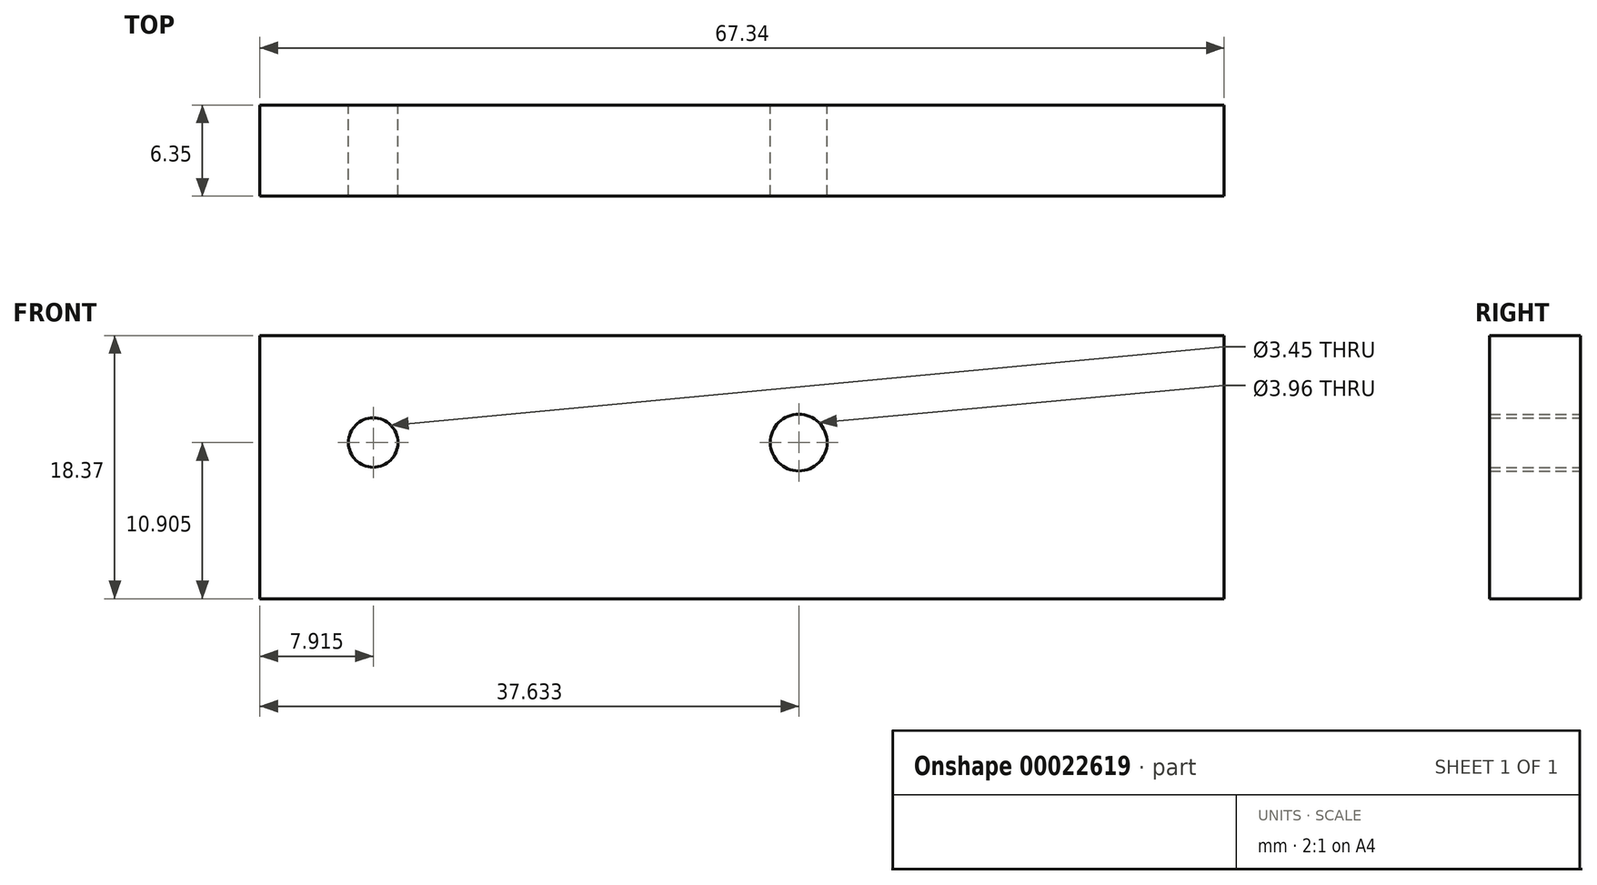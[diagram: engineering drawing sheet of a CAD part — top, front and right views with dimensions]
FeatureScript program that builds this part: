
annotation { "Feature Type Name" : "Feature", "Feature Type Description" : "" }
export const myFeature = defineFeature(function(context is Context, id is Id, definition is map)
    precondition{}
    {
        {
            var Q0;
            Q0=qCreatedBy(makeId("Front.planeOp"),FACE);
            var sketch = newSketch(context, id + "F0", { "sketchPlane" : qUnion([Q0])});
            skCircle(sketch, "E0", {"center": v(-31.44, 26.57) * mm, "radius": 1.73 * mm});
            skCircle(sketch, "E1", {"center": v(-1.72, 26.57) * mm, "radius": 1.98 * mm});
            skLineSegment(sketch, "E2.rect.bottom", {"start": v(-39.35, 34.03) * mm, "end": v(27.99, 34.03) * mm});
            skLineSegment(sketch, "E2.rect.top", {"start": v(-39.35, 15.66) * mm, "end": v(27.99, 15.66) * mm});
            skLineSegment(sketch, "E2.rect.left", {"start": v(-39.35, 34.03) * mm, "end": v(-39.35, 15.66) * mm});
            skLineSegment(sketch, "E2.rect.right", {"start": v(27.99, 34.03) * mm, "end": v(27.99, 15.66) * mm});
            skPoint(sketch, "E2.rect.middle", {"position": v(-5.68, 24.84) * mm});
            skSolve(sketch);
        }
        {
            var Q0;
            Q0 = qSketchRegion(id + "F0", true);
            extrude(context, id + "F1", {"entities" : qUnion([Q0]), "depth" : 6.35 * mm});
        }
    });
